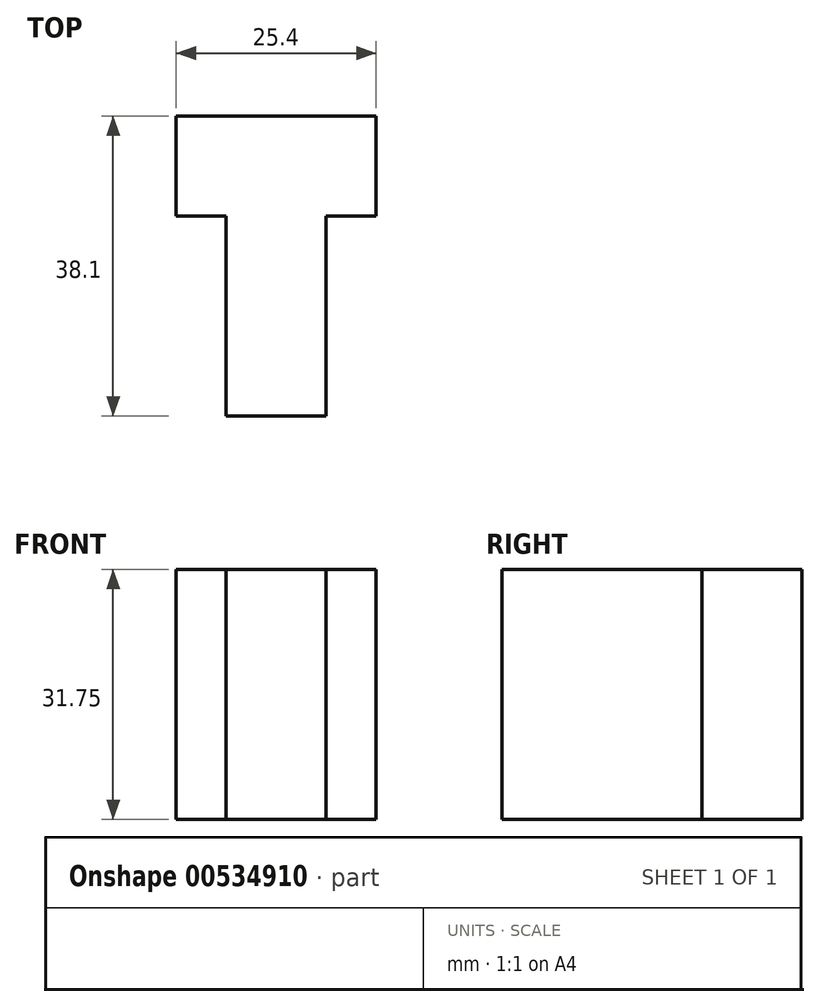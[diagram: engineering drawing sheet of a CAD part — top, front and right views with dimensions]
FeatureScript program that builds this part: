
annotation { "Feature Type Name" : "Feature", "Feature Type Description" : "" }
export const myFeature = defineFeature(function(context is Context, id is Id, definition is map)
    precondition{}
    {
        {
            var Q0;
            Q0=qCreatedBy(makeId("Top.planeOp"),FACE);
            var sketch = newSketch(context, id + "F0", { "sketchPlane" : qUnion([Q0])});
            skLineSegment(sketch, "E0", {"start": v(-59.4, 50.16) * mm, "end": v(-34, 50.16) * mm});
            skLineSegment(sketch, "E1", {"start": v(-34, 50.16) * mm, "end": v(-34, 37.46) * mm});
            skLineSegment(sketch, "E2", {"start": v(-34, 37.46) * mm, "end": v(-40.34, 37.46) * mm});
            skLineSegment(sketch, "E3", {"start": v(-40.34, 37.46) * mm, "end": v(-40.34, 12.06) * mm});
            skLineSegment(sketch, "E4", {"start": v(-40.34, 12.06) * mm, "end": v(-53.04, 12.06) * mm});
            skLineSegment(sketch, "E5", {"start": v(-53.04, 12.06) * mm, "end": v(-53.04, 37.46) * mm});
            skLineSegment(sketch, "E6", {"start": v(-53.04, 37.46) * mm, "end": v(-59.4, 37.46) * mm});
            skLineSegment(sketch, "E7", {"start": v(-59.4, 37.46) * mm, "end": v(-59.4, 50.16) * mm});
            skSolve(sketch);
        }
        {
            var Q0;
            Q0=makeQuery(id+"F0.imprint","IMPRINT",FACE,{"disambiguationData":[TD([[makeQuery(id+"F0.imprint","IMPRINT",EDGE,{"derivedFrom":sQuery(id+"F0.wireOp",EDGE,"E0")}),-1.0]])]});
            extrude(context, id + "F1", {"entities" : qUnion([Q0]), "depth" : 31.75 * mm, "offsetDistance" : 25.4 * mm});
        }
    });
